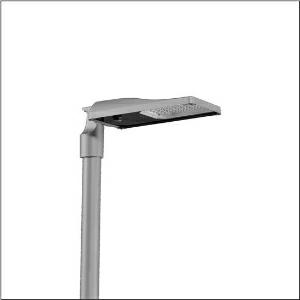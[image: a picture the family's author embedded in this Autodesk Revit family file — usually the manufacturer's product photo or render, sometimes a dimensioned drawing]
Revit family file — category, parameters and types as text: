
# Revit family: streetlight_sl_31_mini___st1_0a_5xh2d3ar08ga_b0cd
name_source: partatom
category: Lighting Fixtures
units: mm (PartAtom-declared; Revit-internal decimal feet)

## family parameters
Cut with Voids When Loaded = No
Host = Face
Light Source = No
Part Type = Normal
Room Calculation Point = No
Round Connector Dimension = Use Diameter
Shared = No

## types (1)
- --- (1 x LED, 5880 lm, 39.3 W, 3000K)
    Apparent Load = 39 VA
    CIE Flux Codes = 37 72 97 100 100
    Color Rendering = 70
    Color Temperature = 3000K
    Default Elevation = 1800 mm
    Description = Streetlight SL 31 mini D4i mast luminaire for post-top, side-entry; light control with lens of PMMA; light distribution: ST1.0a, direct asymmetric distribution, for standard-compliant lighting for roads and squares; LED: luminous flux: 5.880lm, light colour: 730, colour temperature: 3000K; luminous efficacy: 149,6lm/W; control: pre-setting: logarithmic dimming characteristic, flexible luminous flux parameterisation, time-dependent luminous flux control, constant luminous flux control, power reduction, intelligent temperature release in ECG and LED module, overheat protection; luminaire housing, of diecast aluminium, SITECO metallic grey (DB 702S), corrosivity category C5 high according to DIN EN ISO 12944; cover of toughened safety glass, transparent, mast flange of diecast aluminium, SITECO metallic grey (DB 702S), spigot size: 76/60mm, mast flange included unmounted; cable length: 8,5m, connection cable pre-assembled; mains connection: 220..240V, AC, 50/60Hz; power consumption (at start of service life): 39,3W / (at end of service life): 40,7W / (with reduced operation 50%): 18,1W; protection rating (complete): IP66; insulation class (complete): insulation class II (safety insulation); impact resistance: IK09; certification: CE, ENEC, ENEC+, VDE, UKCA, ZD4i; permissible operating ambient temperature for outdoor applications: -40..+50°C; packaging unit: 1 piece

Light Distribution: ST1.0a
    Height = 76 mm
    Lamp = 1 x LED
    Lamp Light Flux = 5880 lm
    Lamp Power = 39.3 W
    Lamp count = 1
    Length = 547 mm
    Luminous efficacy = 150 lm/W
    Manufacturer = Siteco
    ModVariant = No
    Model = 5XH2D3AR08GA
    Number of Poles = 1
    OnlyDefault = Yes
    Power Factor = 1
    Product Name = Streetlight SL 31 mini | ST1.0a
    Product group = mast luminaire | pylon top
    ProductGroupID = 6100
    Protection Class = Protection class II
    Protection Degree = IP 66
    RLX_Detail_Level = 1
    RLX_Emergency_Light_Flux = 0 lm
    RLX_Emergency_Type = 0
    RLX_Emergency_Type_DB = No
    RlxData = <blob elided: 39673 chars, md5=f996621e>
    Socket = socket
    Standby Power = 0 W
    System Light Flux = 5880 lm
    System Power = 39 W
    Type Comments = factory setting: luminous flux: 100 % | dim-lin: 254 | 798 mA
    Type Image = l_1300328.jpg
    URL = http://relux.com
    VarID = @adj_061533
    Voltage = 0 V
    Weight = 0.00 kg
    Width = 265 mm

## geometry (parser evidence)
native form markers: Blend x4, Sweep x11
no freeform markers — native parametric forms only
